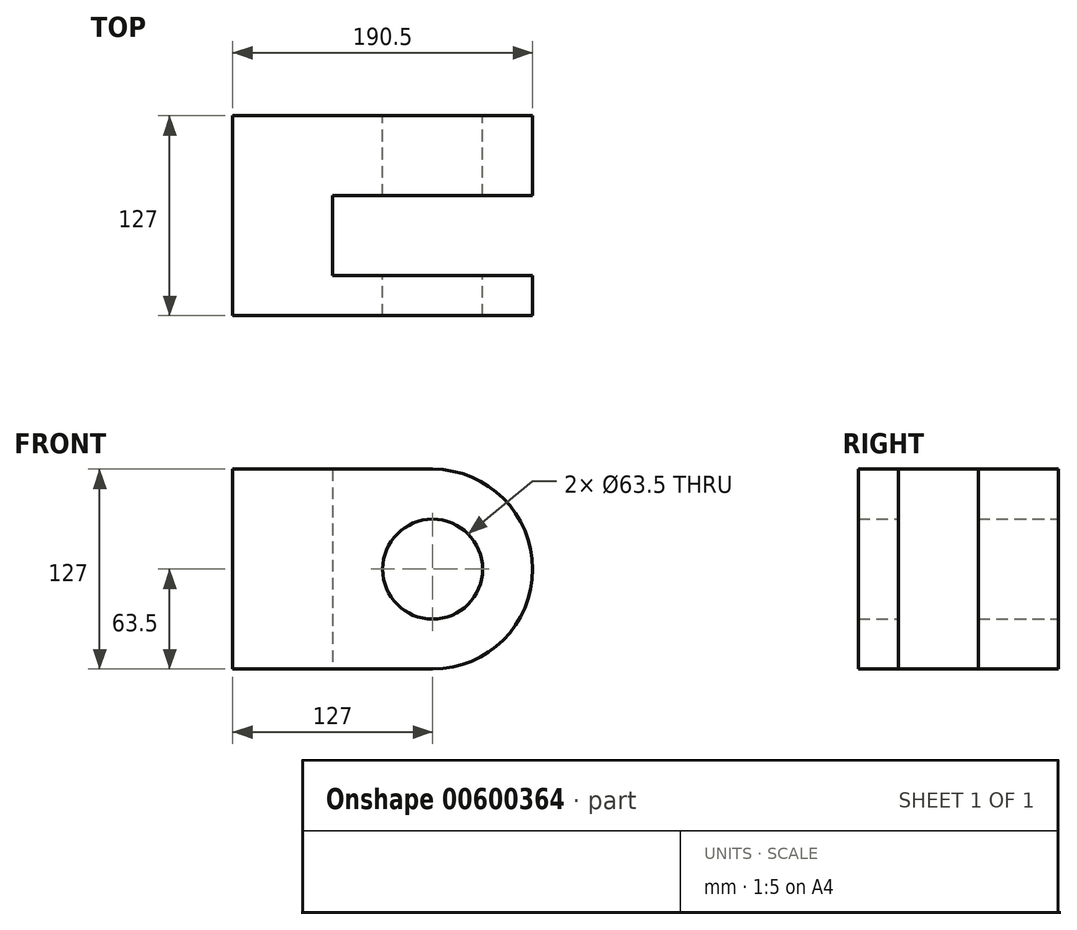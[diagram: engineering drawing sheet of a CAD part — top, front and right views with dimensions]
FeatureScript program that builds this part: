
annotation { "Feature Type Name" : "Feature", "Feature Type Description" : "" }
export const myFeature = defineFeature(function(context is Context, id is Id, definition is map)
    precondition{}
    {
        {
            var Q0;
            Q0=qCreatedBy(makeId("Front.planeOp"),FACE);
            var sketch = newSketch(context, id + "F0", { "sketchPlane" : qUnion([Q0])});
            skCircle(sketch, "E0", {"center": v(0, 0) * mm, "radius": 63.5 * mm});
            skCircle(sketch, "E1", {"center": v(0, 0) * mm, "radius": 31.75 * mm});
            skLineSegment(sketch, "E2", {"start": v(0, 63.5) * mm, "end": v(-127, 63.5) * mm});
            skLineSegment(sketch, "E3", {"start": v(-127, 63.5) * mm, "end": v(-127, -63.5) * mm});
            skLineSegment(sketch, "E4", {"start": v(-127, -63.5) * mm, "end": v(0, -63.5) * mm});
            skSolve(sketch);
        }
        {
            var Q0;
            Q0 = qSketchRegion(id + "F0", true);
            extrude(context, id + "F1", {"entities" : qUnion([Q0]), "depth" : 50.8 * mm, "offsetDistance" : 25.4 * mm});
        }
        {
            var Q0;
            Q0=makeQuery(id+"F1.opExtrude","CAP_FACE",FACE,{"disambiguationData":[OSD([sQuery(id+"F0.wireOp",EDGE,"E0"),sQuery(id+"F0.wireOp",EDGE,"E1"),sQuery(id+"F0.wireOp",EDGE,"E2"),sQuery(id+"F0.wireOp",EDGE,"E3"),sQuery(id+"F0.wireOp",EDGE,"E4")])],"isStart":false});
            cPlane(context, id + "F2", {"entities" : qUnion([Q0]), "cplaneType" : CPlaneType.OFFSET, "offset" : 50.8 * mm, "width" : 152.4 * mm, "height" : 152.4 * mm});
        }
        {
            var Q0;
            Q0=qCreatedBy(id+"F2.planeOp",FACE);
            var sketch = newSketch(context, id + "F3", { "sketchPlane" : qUnion([Q0])});
            skLineSegment(sketch, "E5.0.0", {"start": v(-127, -63.5) * mm, "end": v(0, -63.5) * mm});
            skArc(sketch, "E5.0.1", {"start": v(0, -63.5) * mm, "mid": v(63.5, 0) * mm, "end": v(0, 63.5) * mm});
            skLineSegment(sketch, "E5.0.2", {"start": v(0, 63.5) * mm, "end": v(-127, 63.5) * mm});
            skLineSegment(sketch, "E5.0.3", {"start": v(-127, 63.5) * mm, "end": v(-127, -63.5) * mm});
            skCircle(sketch, "E6.0", {"center": v(0, 0) * mm, "radius": 31.75 * mm});
            skSolve(sketch);
        }
        {
            var Q0;
            Q0=makeQuery(id+"F3.imprint","IMPRINT",FACE,{"disambiguationData":[TD([[makeQuery(id+"F3.imprint","IMPRINT",EDGE,{"derivedFrom":sQuery(id+"F3.wireOp",EDGE,"E5.0.0")}),1.0]])]});
            extrude(context, id + "F4", {"entities" : qUnion([Q0]), "depth" : 25.4 * mm, "offsetDistance" : 25.4 * mm});
        }
        {
            var Q0;
            Q0=makeQuery(id+"F1.opExtrude","CAP_FACE",FACE,{"disambiguationData":[OSD([sQuery(id+"F0.wireOp",EDGE,"E0"),sQuery(id+"F0.wireOp",EDGE,"E1"),sQuery(id+"F0.wireOp",EDGE,"E2"),sQuery(id+"F0.wireOp",EDGE,"E3"),sQuery(id+"F0.wireOp",EDGE,"E4")])],"isStart":false});
            var sketch = newSketch(context, id + "F5", { "sketchPlane" : qUnion([Q0])});
            skLineSegment(sketch, "E7.bottom", {"start": v(-127, 63.5) * mm, "end": v(-63.5, 63.5) * mm});
            skLineSegment(sketch, "E7.top", {"start": v(-127, -63.5) * mm, "end": v(-63.5, -63.5) * mm});
            skLineSegment(sketch, "E7.left", {"start": v(-127, 63.5) * mm, "end": v(-127, -63.5) * mm});
            skLineSegment(sketch, "E7.right", {"start": v(-63.5, 63.5) * mm, "end": v(-63.5, -63.5) * mm});
            skSolve(sketch);
        }
        {
            var Q0;
            Q0=makeQuery(id+"F5.imprint","IMPRINT",FACE,{"disambiguationData":[TD([[makeQuery(id+"F5.imprint","IMPRINT",EDGE,{"derivedFrom":sQuery(id+"F5.wireOp",EDGE,"E7.bottom")}),1.0]])]});
            extrude(context, id + "F6", {"entities" : qUnion([Q0]), "endBound" : BoundingType.UP_TO_NEXT, "depth" : 25.4 * mm, "offsetDistance" : 25.4 * mm});
        }
        {
            var Q0;
            Q0=makeQuery(id+"F1.opExtrude","CAP_FACE",FACE,{"disambiguationData":[OSD([sQuery(id+"F0.wireOp",EDGE,"E0"),sQuery(id+"F0.wireOp",EDGE,"E1"),sQuery(id+"F0.wireOp",EDGE,"E2"),sQuery(id+"F0.wireOp",EDGE,"E3"),sQuery(id+"F0.wireOp",EDGE,"E4")])],"isStart":false});
            var sketch = newSketch(context, id + "F7", { "sketchPlane" : qUnion([Q0])});
            skLineSegment(sketch, "E8.bottom", {"start": v(-127, 63.5) * mm, "end": v(-63.5, 63.5) * mm});
            skLineSegment(sketch, "E8.top", {"start": v(-127, -63.5) * mm, "end": v(-63.5, -63.5) * mm});
            skLineSegment(sketch, "E8.left", {"start": v(-127, 63.5) * mm, "end": v(-127, -63.5) * mm});
            skLineSegment(sketch, "E8.right", {"start": v(-63.5, 63.5) * mm, "end": v(-63.5, -63.5) * mm});
            skSolve(sketch);
        }
        {
            var Q0;
            Q0=makeQuery(id+"F7.imprint","IMPRINT",FACE,{"disambiguationData":[TD([[makeQuery(id+"F7.imprint","IMPRINT",EDGE,{"derivedFrom":sQuery(id+"F7.wireOp",EDGE,"E8.bottom")}),1.0]])]});
            extrude(context, id + "F8", {"entities" : qUnion([Q0]), "operationType" : NewBodyOperationType.ADD, "endBound" : BoundingType.UP_TO_NEXT, "depth" : 25.4 * mm, "offsetDistance" : 25.4 * mm});
        }
    });
